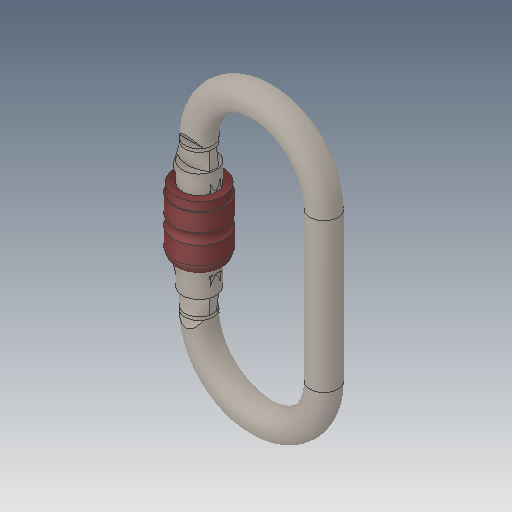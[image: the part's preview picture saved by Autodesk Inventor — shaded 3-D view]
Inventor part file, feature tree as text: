
AUTODESK INVENTOR PART (.ipt)
format: ipt  version: 2023.5 (Build 275446000, 446)  size: 251,392 bytes
history: native  units: in
note: dims shown in document units (in); Inventor stores cm internally (conversion verified against a paired STEP export)
features: fillet x1
ambient origin geometry x8: Origin, YZ Plane, XZ Plane, XY Plane, X Axis, Y Axis, Z Axis, Center Point
bodies: Solid1 (feature_tree)
feature tree (1):
  fillet  "Fillet6"  [1 undecoded]
note: 1 required parameter value undecoded (feature->parameter linkage not recoverable at this tier; creation-order binding heuristic only, values carry confidence <= 0.55)
